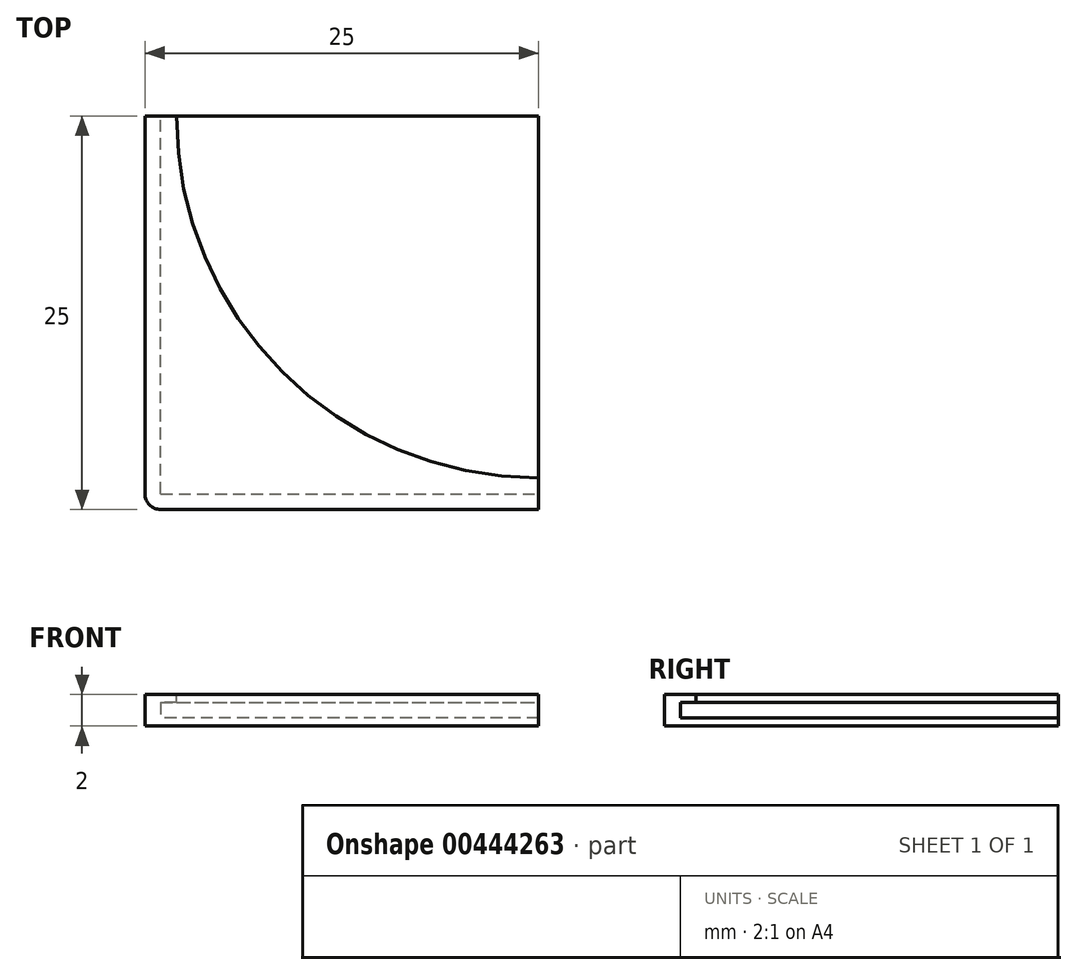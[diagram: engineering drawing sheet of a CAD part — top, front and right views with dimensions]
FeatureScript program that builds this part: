
annotation { "Feature Type Name" : "Feature", "Feature Type Description" : "" }
export const myFeature = defineFeature(function(context is Context, id is Id, definition is map)
    precondition{}
    {
        {
            var Q0;
            Q0=qCreatedBy(makeId("Top.planeOp"),FACE);
            var sketch = newSketch(context, id + "F0", { "sketchPlane" : qUnion([Q0])});
            skLineSegment(sketch, "E0.bottom", {"start": v(12.5, 12.5) * mm, "end": v(-12.5, 12.5) * mm});
            skLineSegment(sketch, "E0.top", {"start": v(12.5, -12.5) * mm, "end": v(-12.5, -12.5) * mm});
            skLineSegment(sketch, "E0.left", {"start": v(12.5, 12.5) * mm, "end": v(12.5, -12.5) * mm});
            skLineSegment(sketch, "E0.right", {"start": v(-12.5, 12.5) * mm, "end": v(-12.5, -12.5) * mm});
            skPoint(sketch, "E0.middle", {"position": v(0, 0) * mm});
            skSolve(sketch);
        }
        {
            var Q0;
            Q0=makeQuery(id+"F0.imprint","IMPRINT",FACE,{"disambiguationData":[TD([[makeQuery(id+"F0.imprint","IMPRINT",EDGE,{"derivedFrom":sQuery(id+"F0.wireOp",EDGE,"E0.bottom")}),1.0]])]});
            extrude(context, id + "F1", {"entities" : qUnion([Q0]), "depth" : 2 * mm});
        }
        {
            var Q0;
            Q0=makeQuery(id+"F1.opExtrude","CAP_FACE",FACE,{"disambiguationData":[OSD([sQuery(id+"F0.wireOp",EDGE,"E0.bottom"),sQuery(id+"F0.wireOp",EDGE,"E0.top"),sQuery(id+"F0.wireOp",EDGE,"E0.left"),sQuery(id+"F0.wireOp",EDGE,"E0.right")])],"isStart":false});
            var sketch = newSketch(context, id + "F2", { "sketchPlane" : qUnion([Q0])});
            skLineSegment(sketch, "E1.0", {"start": v(12.5, 12.5) * mm, "end": v(-10.5, 12.5) * mm});
            skLineSegment(sketch, "E2.0", {"start": v(12.5, 12.5) * mm, "end": v(12.5, -10.5) * mm});
            skArc(sketch, "E3", {"start": v(-10.5, 12.5) * mm, "mid": v(-3.76, -3.76) * mm, "end": v(12.5, -10.5) * mm});
            skPoint(sketch, "E4.orphan", {"position": v(12.5, -12.5) * mm});
            skPoint(sketch, "E5.orphan", {"position": v(-12.5, 12.5) * mm});
            skSolve(sketch);
        }
        {
            var Q0;
            Q0 = qSketchRegion(id + "F2", true);
            extrude(context, id + "F3", {"entities" : qUnion([Q0]), "operationType" : NewBodyOperationType.REMOVE, "oppositeDirection" : true, "depth" : 1.5 * mm});
        }
        {
            var Q0;
            Q0=makeQuery(id+"F3.boolean.opBoolean","COPY",FACE,{"derivedFrom":makeQuery(id+"F3.opExtrude","CAP_FACE",FACE,{"disambiguationData":[OSD([sQuery(id+"F2.wireOp",EDGE,"E1.0"),sQuery(id+"F2.wireOp",EDGE,"E2.0"),sQuery(id+"F2.wireOp",EDGE,"E3")])],"isStart":false})});
            var sketch = newSketch(context, id + "F4", { "sketchPlane" : qUnion([Q0])});
            skLineSegment(sketch, "E6.bottom", {"start": v(-11.5, -11.5) * mm, "end": v(15.87, -11.5) * mm});
            skLineSegment(sketch, "E6.top", {"start": v(-11.5, 16.66) * mm, "end": v(15.87, 16.66) * mm});
            skLineSegment(sketch, "E6.left", {"start": v(-11.5, -11.5) * mm, "end": v(-11.5, 16.66) * mm});
            skLineSegment(sketch, "E6.right", {"start": v(15.87, -11.5) * mm, "end": v(15.87, 16.66) * mm});
            skSolve(sketch);
        }
        {
            var Q0;
            Q0 = qSketchRegion(id + "F4", true);
            extrude(context, id + "F5", {"entities" : qUnion([Q0]), "operationType" : NewBodyOperationType.REMOVE, "depth" : 1 * mm});
        }
        {
            var Q0;
            Q0=makeQuery(id+"F1.opExtrude","SWEPT_EDGE",EDGE,{"disambiguationData":[OSD([sQuery(id+"F0.wireOp",EDGE,"E0.top"),sQuery(id+"F0.wireOp",EDGE,"E0.right")])]});
            fillet(context, id + "F6", {"entities" : qUnion([Q0]), "radius" : 1 * mm, "tangentPropagation" : true, "allowEdgeOverflow" : false});
        }
    });
